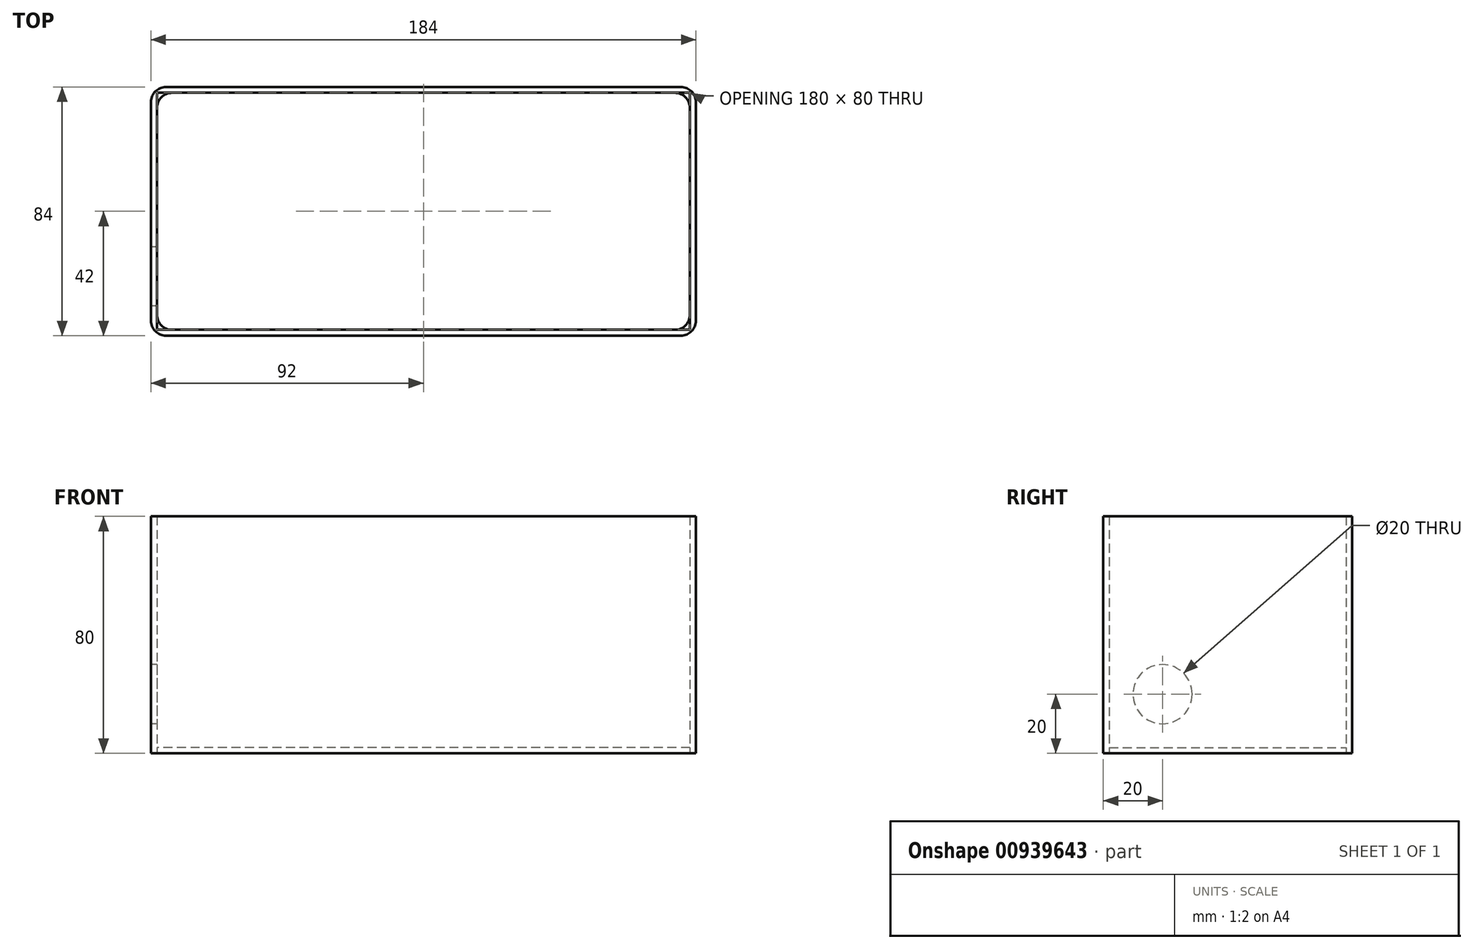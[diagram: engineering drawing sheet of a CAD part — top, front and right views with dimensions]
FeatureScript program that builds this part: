
annotation { "Feature Type Name" : "Feature", "Feature Type Description" : "" }
export const myFeature = defineFeature(function(context is Context, id is Id, definition is map)
    precondition{}
    {
        {
            var Q0;
            Q0=qCreatedBy(makeId("Top.planeOp"),FACE);
            var sketch = newSketch(context, id + "F0", { "sketchPlane" : qUnion([Q0])});
            skLineSegment(sketch, "E0.bottom", {"start": v(-90, -40) * mm, "end": v(90, -40) * mm});
            skLineSegment(sketch, "E0.top", {"start": v(-90, 40) * mm, "end": v(90, 40) * mm});
            skLineSegment(sketch, "E0.left", {"start": v(-90, -40) * mm, "end": v(-90, 40) * mm});
            skLineSegment(sketch, "E0.right", {"start": v(90, -40) * mm, "end": v(90, 40) * mm});
            skPoint(sketch, "E0.middle", {"position": v(0, 0) * mm});
            skLineSegment(sketch, "E1.0", {"start": v(92, -42) * mm, "end": v(92, 42) * mm});
            skLineSegment(sketch, "E1.1", {"start": v(-92, -42) * mm, "end": v(92, -42) * mm});
            skLineSegment(sketch, "E1.2", {"start": v(-92, -42) * mm, "end": v(-92, 42) * mm});
            skLineSegment(sketch, "E1.3", {"start": v(-92, 42) * mm, "end": v(92, 42) * mm});
            skSolve(sketch);
        }
        {
            var Q0;
            Q0=makeQuery(id+"F0.imprint","IMPRINT",FACE,{"disambiguationData":[TD([[makeQuery(id+"F0.imprint","IMPRINT",EDGE,{"derivedFrom":sQuery(id+"F0.wireOp",EDGE,"E0.bottom")}),-1.0]])]});
            extrude(context, id + "F1", {"entities" : qUnion([Q0]), "depth" : 80 * mm, "offsetDistance" : 25.4 * mm});
        }
        {
            var Q0;
            Q0=qCreatedBy(makeId("Right.planeOp"),FACE);
            var sketch = newSketch(context, id + "F2", { "sketchPlane" : qUnion([Q0])});
            skLineSegment(sketch, "E2.bottom", {"start": v(-40, 0) * mm, "end": v(40, 0) * mm});
            skLineSegment(sketch, "E2.top", {"start": v(-40, 2) * mm, "end": v(40, 2) * mm});
            skLineSegment(sketch, "E2.left", {"start": v(-40, 2) * mm, "end": v(-40, 0) * mm});
            skLineSegment(sketch, "E2.right", {"start": v(40, 2) * mm, "end": v(40, 0) * mm});
            skPoint(sketch, "E2.middle", {"position": v(0, 1) * mm});
            skSolve(sketch);
        }
        {
            var Q0;
            Q0 = qSketchRegion(id + "F2", true);
            extrude(context, id + "F3", {"entities" : qUnion([Q0]), "endBound" : BoundingType.SYMMETRIC, "depth" : 180 * mm, "offsetDistance" : 25.4 * mm});
        }
        {
            var Q0;
            Q0=makeQuery(id+"F1.opExtrude","SWEPT_FACE",FACE,{"disambiguationData":[OSD([sQuery(id+"F0.wireOp",EDGE,"E1.2")])]});
            var sketch = newSketch(context, id + "F4", { "sketchPlane" : qUnion([Q0])});
            skCircle(sketch, "E3", {"center": v(22, 20) * mm, "radius": 10 * mm});
            skSolve(sketch);
        }
        {
            var Q0;
            Q0=makeQuery(id+"F4.imprint","IMPRINT",FACE,{"disambiguationData":[TD([[makeQuery(id+"F4.imprint","IMPRINT",EDGE,{"derivedFrom":sQuery(id+"F4.wireOp",EDGE,"E3")}),1.0]])]});
            extrude(context, id + "F5", {"entities" : qUnion([Q0]), "operationType" : NewBodyOperationType.REMOVE, "oppositeDirection" : true, "depth" : 2 * mm, "offsetDistance" : 25.4 * mm});
        }
        {
            var Q0;
            Q0=makeQuery(id+"F1.opExtrude","SWEPT_EDGE",EDGE,{"disambiguationData":[OSD([sQuery(id+"F0.wireOp",EDGE,"E1.1"),sQuery(id+"F0.wireOp",EDGE,"E1.2")])]});
            var Q1;
            Q1=makeQuery(id+"F1.opExtrude","SWEPT_EDGE",EDGE,{"disambiguationData":[OSD([sQuery(id+"F0.wireOp",EDGE,"E0.bottom"),sQuery(id+"F0.wireOp",EDGE,"E0.left")])]});
            var Q2;
            Q2=makeQuery(id+"F1.opExtrude","SWEPT_EDGE",EDGE,{"disambiguationData":[OSD([sQuery(id+"F0.wireOp",EDGE,"E1.2"),sQuery(id+"F0.wireOp",EDGE,"E1.3")])]});
            var Q3;
            Q3=makeQuery(id+"F1.opExtrude","SWEPT_EDGE",EDGE,{"disambiguationData":[OSD([sQuery(id+"F0.wireOp",EDGE,"E0.top"),sQuery(id+"F0.wireOp",EDGE,"E0.left")])]});
            var Q4;
            Q4=makeQuery(id+"F1.opExtrude","SWEPT_EDGE",EDGE,{"disambiguationData":[OSD([sQuery(id+"F0.wireOp",EDGE,"E0.top"),sQuery(id+"F0.wireOp",EDGE,"E0.right")])]});
            var Q5;
            Q5=makeQuery(id+"F1.opExtrude","SWEPT_EDGE",EDGE,{"disambiguationData":[OSD([sQuery(id+"F0.wireOp",EDGE,"E1.0"),sQuery(id+"F0.wireOp",EDGE,"E1.3")])]});
            var Q6;
            Q6=makeQuery(id+"F1.opExtrude","SWEPT_EDGE",EDGE,{"disambiguationData":[OSD([sQuery(id+"F0.wireOp",EDGE,"E1.0"),sQuery(id+"F0.wireOp",EDGE,"E1.1")])]});
            var Q7;
            Q7=makeQuery(id+"F1.opExtrude","SWEPT_EDGE",EDGE,{"disambiguationData":[OSD([sQuery(id+"F0.wireOp",EDGE,"E0.bottom"),sQuery(id+"F0.wireOp",EDGE,"E0.right")])]});
            fillet(context, id + "F6", {"entities" : qUnion([Q0, Q1, Q2, Q3, Q4, Q5, Q6, Q7]), "radius" : 5.08 * mm, "tangentPropagation" : true, "allowEdgeOverflow" : false});
        }
    });
